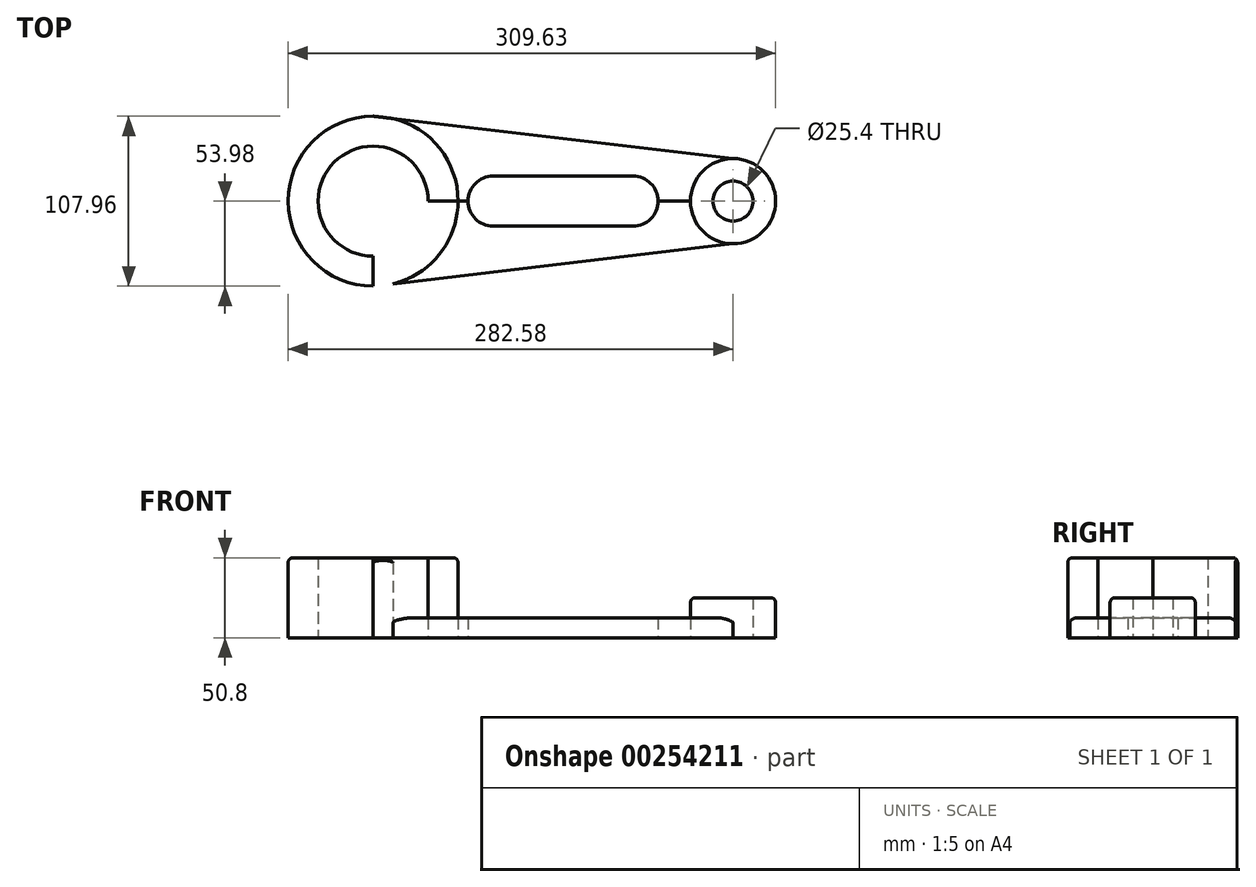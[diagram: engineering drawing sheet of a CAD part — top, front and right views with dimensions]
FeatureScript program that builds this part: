
annotation { "Feature Type Name" : "Feature", "Feature Type Description" : "" }
export const myFeature = defineFeature(function(context is Context, id is Id, definition is map)
    precondition{}
    {
        {
            var Q0;
            Q0=qCreatedBy(makeId("Top.planeOp"),FACE);
            var sketch = newSketch(context, id + "F0", { "sketchPlane" : qUnion([Q0])});
            skLineSegment(sketch, "E0", {"start": v(0, 0) * mm, "end": v(-44.45, 0) * mm});
            skLineSegment(sketch, "E1", {"start": v(0, 0) * mm, "end": v(44.45, 0) * mm});
            skLineSegment(sketch, "E2", {"start": v(-44.45, 0) * mm, "end": v(-120.65, 0) * mm});
            skCircle(sketch, "E3", {"center": v(-120.65, 0) * mm, "radius": 34.93 * mm});
            skCircle(sketch, "E4", {"center": v(-120.65, 0) * mm, "radius": 53.98 * mm});
            skLineSegment(sketch, "E5", {"start": v(-120.65, 0) * mm, "end": v(107.95, 0) * mm});
            skCircle(sketch, "E6", {"center": v(107.95, 0) * mm, "radius": 12.7 * mm});
            skCircle(sketch, "E7", {"center": v(107.95, 0) * mm, "radius": 27.05 * mm});
            skLineSegment(sketch, "E8", {"start": v(-120.65, 0) * mm, "end": v(-120.65, -53.98) * mm});
            skLineSegment(sketch, "E9", {"start": v(-120.65, -53.98) * mm, "end": v(-120.65, 53.98) * mm});
            skLineSegment(sketch, "E10", {"start": v(107.95, 0) * mm, "end": v(107.95, -27.05) * mm});
            skLineSegment(sketch, "E11", {"start": v(107.95, -27.05) * mm, "end": v(107.95, 27.05) * mm});
            skLineSegment(sketch, "E12", {"start": v(-120.65, -53.97) * mm, "end": v(107.95, -27.05) * mm});
            skLineSegment(sketch, "E13", {"start": v(107.95, 27.05) * mm, "end": v(-120.65, 53.97) * mm});
            skArc(sketch, "E14", {"start": v(-44.45, 15.88) * mm, "mid": v(-60.33, 0) * mm, "end": v(-44.45, -15.88) * mm});
            skArc(sketch, "E15", {"start": v(44.45, -15.88) * mm, "mid": v(60.33, 0) * mm, "end": v(44.45, 15.88) * mm});
            skLineSegment(sketch, "E16", {"start": v(-44.45, 15.88) * mm, "end": v(-44.45, -15.88) * mm});
            skLineSegment(sketch, "E17", {"start": v(-44.45, -15.88) * mm, "end": v(44.45, -15.88) * mm});
            skLineSegment(sketch, "E18", {"start": v(44.45, -15.88) * mm, "end": v(44.45, 15.88) * mm});
            skLineSegment(sketch, "E19", {"start": v(44.45, 15.88) * mm, "end": v(-44.45, 15.88) * mm});
            skPoint(sketch, "E20.end.orphan", {"position": v(0, 15.88) * mm});
            skPoint(sketch, "E21.MirrorCS.end.orphan", {"position": v(0, -15.88) * mm});
            skPoint(sketch, "E21.MirrorCS.start.orphan", {"position": v(0, 0) * mm});
            skSolve(sketch);
        }
        {
            var Q0;
            {var subQ0=sQuery(id+"F0.wireOp",EDGE,"E9");var subQ1=sQuery(id+"F0.wireOp",EDGE,"E3");var subQ2=makeQuery(id+"F0.imprint","INTERSECT",VERTEX,{"disambiguationData":[OD(0.0)],"derivedFrom":[subQ1,subQ0]});Q0=makeQuery(id+"F0.imprint","IMPRINT",FACE,{"disambiguationData":[TD([[makeQuery(id+"F0.imprint","IMPRINT",EDGE,{"disambiguationData":[TD([[subQ2,-1.0]])],"derivedFrom":subQ1}),-1.0]])]});}
            var Q1;
            {var subQ1=sQuery(id+"F0.wireOp",EDGE,"E9");var subQ4=sQuery(id+"F0.wireOp",EDGE,"E3");var subQ5=makeQuery(id+"F0.imprint","INTERSECT",VERTEX,{"disambiguationData":[OD(0.0)],"derivedFrom":[subQ4,subQ1]});Q1=makeQuery(id+"F0.imprint","IMPRINT",FACE,{"disambiguationData":[TD([[makeQuery(id+"F0.imprint","IMPRINT",EDGE,{"disambiguationData":[TD([[subQ5,1.0]])],"derivedFrom":subQ4}),-1.0]])]});}
            var Q2;
            {var subQ0=sQuery(id+"F0.wireOp",EDGE,"E5");var subQ1=sQuery(id+"F0.wireOp",EDGE,"E3");var subQ2=makeQuery(id+"F0.imprint","INTERSECT",VERTEX,{"derivedFrom":[subQ1,subQ0]});Q2=makeQuery(id+"F0.imprint","IMPRINT",FACE,{"disambiguationData":[TD([[makeQuery(id+"F0.imprint","IMPRINT",EDGE,{"disambiguationData":[TD([[subQ2,1.0]])],"derivedFrom":subQ1}),-1.0]])]});}
            extrude(context, id + "F1", {"entities" : qUnion([Q0, Q1, Q2]), "depth" : 50.8 * mm});
        }
        {
            var Q0;
            {var subQ0=sQuery(id+"F0.wireOp",EDGE,"E11");var subQ1=sQuery(id+"F0.wireOp",EDGE,"E6");var subQ2=makeQuery(id+"F0.imprint","INTERSECT",VERTEX,{"disambiguationData":[OD(0.0)],"derivedFrom":[subQ1,subQ0]});Q0=makeQuery(id+"F0.imprint","IMPRINT",FACE,{"disambiguationData":[TD([[makeQuery(id+"F0.imprint","IMPRINT",EDGE,{"disambiguationData":[TD([[subQ2,1.0]])],"derivedFrom":subQ1}),-1.0]])]});}
            extrude(context, id + "F2", {"entities" : qUnion([Q0]), "depth" : 25.4 * mm});
        }
        {
            var Q0;
            {var subQ0=sQuery(id+"F0.wireOp",EDGE,"E7");var subQ1=sQuery(id+"F0.wireOp",EDGE,"E5");var subQ2=makeQuery(id+"F0.imprint","INTERSECT",VERTEX,{"derivedFrom":[subQ1,subQ0]});Q0=makeQuery(id+"F0.imprint","IMPRINT",FACE,{"disambiguationData":[TD([[makeQuery(id+"F0.imprint","IMPRINT",EDGE,{"disambiguationData":[TD([[subQ2,-1.0]])],"derivedFrom":subQ1}),1.0]])]});}
            extrude(context, id + "F3", {"entities" : qUnion([Q0]), "operationType" : NewBodyOperationType.ADD, "depth" : 25.4 * mm});
        }
        {
            var Q0;
            {var subQ0=sQuery(id+"F0.wireOp",EDGE,"E7");var subQ1=sQuery(id+"F0.wireOp",EDGE,"E5");var subQ2=makeQuery(id+"F0.imprint","INTERSECT",VERTEX,{"derivedFrom":[subQ1,subQ0]});Q0=makeQuery(id+"F0.imprint","IMPRINT",FACE,{"disambiguationData":[TD([[makeQuery(id+"F0.imprint","IMPRINT",EDGE,{"disambiguationData":[TD([[subQ2,-1.0]])],"derivedFrom":subQ1}),-1.0]])]});}
            extrude(context, id + "F4", {"entities" : qUnion([Q0]), "operationType" : NewBodyOperationType.ADD, "depth" : 25.4 * mm});
        }
        {
            var Q0;
            {var subQ11=sQuery(id+"F0.wireOp",EDGE,"E17");Q0=makeQuery(id+"F0.imprint","IMPRINT",FACE,{"disambiguationData":[TD([[makeQuery(id+"F0.imprint","IMPRINT",EDGE,{"derivedFrom":subQ11}),-1.0]])]});}
            extrude(context, id + "F5", {"entities" : qUnion([Q0]), "depth" : 12.7 * mm});
        }
        {
            var Q0;
            {var subQ12=sQuery(id+"F0.wireOp",EDGE,"E19");Q0=makeQuery(id+"F0.imprint","IMPRINT",FACE,{"disambiguationData":[TD([[makeQuery(id+"F0.imprint","IMPRINT",EDGE,{"derivedFrom":subQ12}),-1.0]])]});}
            extrude(context, id + "F6", {"entities" : qUnion([Q0]), "depth" : 12.7 * mm});
        }
        {
            var Q0;
            {var subQ0=sQuery(id+"F0.wireOp",EDGE,"E4");Q0=makeQuery(id+"F1.opExtrude","CAP_EDGE",EDGE,{"disambiguationData":[OSD([subQ0]),TDD([makeQuery(id+"F0.imprint","IMPRINT",EDGE,{"disambiguationData":[TD([[makeQuery(id+"F0.imprint","INTERSECT",VERTEX,{"derivedFrom":[subQ0,sQuery(id+"F0.wireOp",EDGE,"E13")]}),1.0]])],"derivedFrom":subQ0}),makeQuery(id+"F0.imprint","IMPRINT",EDGE,{"disambiguationData":[TD([[makeQuery(id+"F0.imprint","INTERSECT",VERTEX,{"derivedFrom":[subQ0,sQuery(id+"F0.wireOp",EDGE,"E12")]}),-1.0]])],"derivedFrom":subQ0})])],"isStart":false});}
            fillet(context, id + "F7", {"entities" : qUnion([Q0]), "radius" : 3.17 * mm, "tangentPropagation" : true, "allowEdgeOverflow" : false});
        }
        {
            var Q0;
            {var subQ0=sQuery(id+"F0.wireOp",EDGE,"E7");Q0=makeQuery(id+"F4.boolean.opBoolean","MERGE",EDGE,{"derivedFrom":[makeQuery(id+"F3.boolean.opBoolean","MERGE",EDGE,{"derivedFrom":[makeQuery(id+"F2.opExtrude","CAP_EDGE",EDGE,{"disambiguationData":[OSD([subQ0])],"isStart":false}),makeQuery(id+"F3.opExtrude","CAP_EDGE",EDGE,{"disambiguationData":[OSD([subQ0])],"isStart":false})]}),makeQuery(id+"F4.opExtrude","CAP_EDGE",EDGE,{"disambiguationData":[OSD([subQ0])],"isStart":false})]});}
            fillet(context, id + "F8", {"entities" : qUnion([Q0]), "radius" : 3.17 * mm, "tangentPropagation" : true, "allowEdgeOverflow" : false});
        }
        {
            var Q0;
            Q0=makeQuery(id+"F5.opExtrude","CAP_EDGE",EDGE,{"disambiguationData":[OSD([sQuery(id+"F0.wireOp",EDGE,"E12")])],"isStart":false});
            fillet(context, id + "F9", {"entities" : qUnion([Q0]), "radius" : 3.17 * mm, "tangentPropagation" : true, "allowEdgeOverflow" : false});
        }
        {
            var Q0;
            Q0=makeQuery(id+"F6.opExtrude","CAP_EDGE",EDGE,{"disambiguationData":[OSD([sQuery(id+"F0.wireOp",EDGE,"E13")])],"isStart":false});
            fillet(context, id + "F10", {"entities" : qUnion([Q0]), "radius" : 3.17 * mm, "tangentPropagation" : true, "allowEdgeOverflow" : false});
        }
    });
